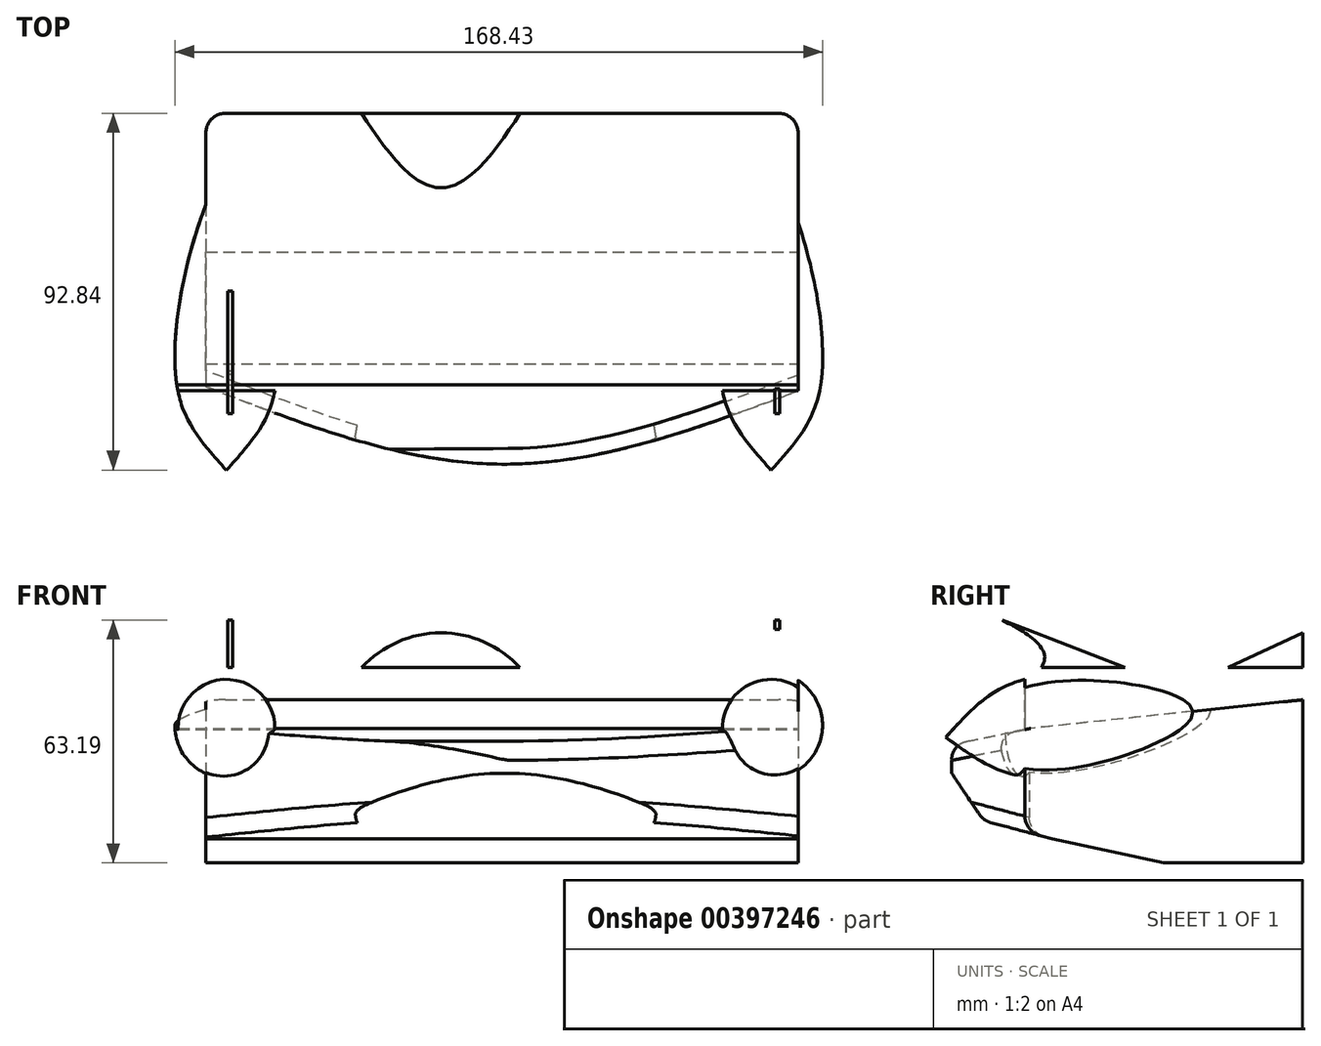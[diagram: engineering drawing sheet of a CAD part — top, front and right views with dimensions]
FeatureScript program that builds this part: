
annotation { "Feature Type Name" : "Feature", "Feature Type Description" : "" }
export const myFeature = defineFeature(function(context is Context, id is Id, definition is map)
    precondition{}
    {
        {
            var Q0;
            Q0=qCreatedBy(makeId("Top.planeOp"),FACE);
            var sketch = newSketch(context, id + "F0", { "sketchPlane" : qUnion([Q0])});
            skLineSegment(sketch, "E0.bottom", {"start": v(-78.1, 78.43) * mm, "end": v(75.9, 78.43) * mm});
            skLineSegment(sketch, "E0.top", {"start": v(-78.1, -12.86) * mm, "end": v(75.9, -12.86) * mm});
            skLineSegment(sketch, "E0.left", {"start": v(-78.1, 78.43) * mm, "end": v(-78.1, -12.86) * mm});
            skLineSegment(sketch, "E0.right", {"start": v(75.9, 78.43) * mm, "end": v(75.9, -12.86) * mm});
            skPoint(sketch, "E1", {"position": v(-1.1, -12.86) * mm});
            skFitSpline(sketch, "E2", {"points": [v(75.9, 6.2) * mm, v(-1.1, -12.86) * mm, v(-78.1, 7.33) * mm], "startDerivative": vector(-154.2, -57.78) * mm, "endDerivative": vector(-153.8, 60) * mm});
            skSolve(sketch);
        }
        {
            var Q0;
            Q0=makeQuery(id+"F0.imprint","IMPRINT",FACE,{"disambiguationData":[TD([[makeQuery(id+"F0.imprint","IMPRINT",EDGE,{"derivedFrom":sQuery(id+"F0.wireOp",EDGE,"E0.bottom")}),-1.0]])]});
            extrude(context, id + "F1", {"entities" : qUnion([Q0]), "depth" : 50.8 * mm});
        }
        {
            var Q0;
            Q0=makeQuery(id+"F1.opExtrude","SWEPT_FACE",FACE,{"disambiguationData":[OSD([sQuery(id+"F0.wireOp",EDGE,"E0.right")])]});
            var sketch = newSketch(context, id + "F2", { "sketchPlane" : qUnion([Q0])});
            skLineSegment(sketch, "E3.bottom", {"start": v(-17.29, 100.9) * mm, "end": v(100.26, 100.9) * mm});
            skLineSegment(sketch, "E3.top", {"start": v(-17.29, -25.48) * mm, "end": v(100.26, -25.48) * mm});
            skLineSegment(sketch, "E3.left", {"start": v(-17.29, 100.9) * mm, "end": v(-17.29, -25.48) * mm});
            skLineSegment(sketch, "E3.right", {"start": v(100.26, 100.9) * mm, "end": v(100.26, -25.48) * mm});
            skLineSegment(sketch, "E4", {"start": v(81.46, 42.76) * mm, "end": v(7.74, 35) * mm});
            skLineSegment(sketch, "E5", {"start": v(13.3, 6.25) * mm, "end": v(42.32, 0) * mm});
            skLineSegment(sketch, "E6", {"start": v(81.46, 42.76) * mm, "end": v(100.26, 42.76) * mm});
            skLineSegment(sketch, "E7", {"start": v(42.32, 0) * mm, "end": v(100.26, 0) * mm});
            skLineSegment(sketch, "E8", {"start": v(7.74, 35) * mm, "end": v(-17.29, 29.94) * mm});
            skLineSegment(sketch, "E9", {"start": v(-17.29, 29.94) * mm, "end": v(-4.57, 11.01) * mm});
            skLineSegment(sketch, "E10", {"start": v(-4.57, 11.01) * mm, "end": v(13.3, 6.25) * mm});
            skSolve(sketch);
        }
        {
            var Q0;
            {var subQ1=sQuery(id+"F2.wireOp",EDGE,"E3.bottom");Q0=makeQuery(id+"F2.imprint","IMPRINT",FACE,{"disambiguationData":[TD([[makeQuery(id+"F2.imprint","IMPRINT",EDGE,{"derivedFrom":subQ1}),-1.0]])]});}
            var Q1;
            {var subQ1=sQuery(id+"F2.wireOp",EDGE,"E3.top");Q1=makeQuery(id+"F2.imprint","IMPRINT",FACE,{"disambiguationData":[TD([[makeQuery(id+"F2.imprint","IMPRINT",EDGE,{"derivedFrom":subQ1}),1.0]])]});}
            var Q2;
            {var subQ0=sQuery(id+"F0.wireOp",EDGE,"E0.right");var subQ1=makeQuery(id+"F1.opExtrude","CAP_EDGE",EDGE,{"disambiguationData":[OSD([subQ0])],"isStart":false});Q2=makeQuery(id+"F2.imprint","IMPRINT",FACE,{"disambiguationData":[TD([[makeQuery(id+"F2.imprint","IMPRINT",EDGE,{"derivedFrom":subQ1}),1.0]])]});}
            var Q3;
            {var subQ0=sQuery(id+"F2.wireOp",EDGE,"E5");Q3=makeQuery(id+"F2.imprint","IMPRINT",FACE,{"disambiguationData":[TD([[makeQuery(id+"F2.imprint","IMPRINT",EDGE,{"derivedFrom":subQ0}),-1.0]])]});}
            extrude(context, id + "F3", {"entities" : qUnion([Q0, Q1, Q2, Q3]), "operationType" : NewBodyOperationType.REMOVE, "oppositeDirection" : true, "depth" : 177.8 * mm});
        }
        {
            var Q0;
            {var subQ0=sQuery(id+"F0.wireOp",EDGE,"E2");Q0=makeQuery(id+"F3.boolean.opBoolean","INTERSECT",EDGE,{"derivedFrom":[makeQuery(id+"F1.opExtrude","SWEPT_FACE",FACE,{"disambiguationData":[OSD([subQ0]),TDD([makeQuery(id+"F0.imprint","IMPRINT",EDGE,{"disambiguationData":[TD([[makeQuery(id+"F0.imprint","INTERSECT",VERTEX,{"derivedFrom":[sQuery(id+"F0.wireOp",EDGE,"E0.right"),subQ0]}),-1.0]])],"derivedFrom":subQ0})])]}),makeQuery(id+"F3.opExtrude","SWEPT_FACE",FACE,{"disambiguationData":[OSD([sQuery(id+"F2.wireOp",EDGE,"E8")])]})]});}
            var Q1;
            {var subQ0=sQuery(id+"F0.wireOp",EDGE,"E2");Q1=makeQuery(id+"F3.boolean.opBoolean","INTERSECT",EDGE,{"derivedFrom":[makeQuery(id+"F1.opExtrude","SWEPT_FACE",FACE,{"disambiguationData":[OSD([subQ0]),TDD([makeQuery(id+"F0.imprint","IMPRINT",EDGE,{"disambiguationData":[TD([[makeQuery(id+"F0.imprint","INTERSECT",VERTEX,{"derivedFrom":[sQuery(id+"F0.wireOp",EDGE,"E0.right"),subQ0]}),-1.0]])],"derivedFrom":subQ0})])]}),makeQuery(id+"F3.opExtrude","SWEPT_FACE",FACE,{"disambiguationData":[OSD([sQuery(id+"F2.wireOp",EDGE,"E10")])]})]});}
            var Q2;
            {var subQ0=sQuery(id+"F0.wireOp",EDGE,"E2");Q2=makeQuery(id+"F3.boolean.opBoolean","INTERSECT",EDGE,{"derivedFrom":[makeQuery(id+"F1.opExtrude","SWEPT_FACE",FACE,{"disambiguationData":[OSD([subQ0]),TDD([makeQuery(id+"F0.imprint","IMPRINT",EDGE,{"disambiguationData":[TD([[makeQuery(id+"F0.imprint","INTERSECT",VERTEX,{"derivedFrom":[sQuery(id+"F0.wireOp",EDGE,"E0.left"),subQ0]}),1.0]])],"derivedFrom":subQ0})])]}),makeQuery(id+"F3.opExtrude","SWEPT_FACE",FACE,{"disambiguationData":[OSD([sQuery(id+"F2.wireOp",EDGE,"E10")])]})]});}
            var Q3;
            Q3=makeQuery(id+"F3.boolean.opBoolean","COPY",EDGE,{"derivedFrom":makeQuery(id+"F3.opExtrude","SWEPT_EDGE",EDGE,{"disambiguationData":[OSD([sQuery(id+"F2.wireOp",EDGE,"E9"),sQuery(id+"F2.wireOp",EDGE,"E10")])]})});
            fillet(context, id + "F4", {"entities" : qUnion([Q0, Q1, Q2, Q3]), "radius" : 5.08 * mm, "tangentPropagation" : true, "allowEdgeOverflow" : false});
        }
        {
            var Q0;
            Q0=makeQuery(id+"F3.boolean.opBoolean","COPY",FACE,{"derivedFrom":makeQuery(id+"F3.opExtrude","SWEPT_FACE",FACE,{"disambiguationData":[OSD([sQuery(id+"F2.wireOp",EDGE,"E4")])]})});
            cPlane(context, id + "F5", {"entities" : qUnion([Q0]), "cplaneType" : CPlaneType.OFFSET, "offset" : 0 * mm, "oppositeDirection" : true, "width" : 152.4 * mm, "height" : 152.4 * mm});
        }
        {
            var Q0;
            Q0=qCreatedBy(id+"F5.planeOp",FACE);
            var sketch = newSketch(context, id + "F6", { "sketchPlane" : qUnion([Q0])});
            skLineSegment(sketch, "E11", {"start": v(-72.76, -10.91) * mm, "end": v(-72.76, 70.39) * mm});
            skFitSpline(sketch, "E12", {"points": [v(-72.76, 70.39) * mm, v(-85.7, 11.75) * mm, v(-72.76, -10.91) * mm], "startDerivative": vector(-49.44, -94.28) * mm, "endDerivative": vector(53.11, -59.52) * mm});
            skLineSegment(sketch, "E13", {"start": v(-1.95, 81.76) * mm, "end": v(-1.95, 38.21) * mm});
            skLineSegment(sketch, "E14.MirrorCS", {"start": v(68.85, -10.91) * mm, "end": v(68.85, 70.39) * mm});
            skFitSpline(sketch, "E15.MirrorCS", {"points": [v(68.85, 70.39) * mm, v(81.8, 11.75) * mm, v(68.85, -10.91) * mm], "startDerivative": vector(49.44, -94.28) * mm, "endDerivative": vector(-53.11, -59.52) * mm});
            skSolve(sketch);
        }
        {
            var Q0;
            Q0=makeQuery(id+"F6.imprint","IMPRINT",FACE,{"disambiguationData":[TD([[makeQuery(id+"F6.imprint","IMPRINT",EDGE,{"derivedFrom":sQuery(id+"F6.wireOp",EDGE,"E11")}),1.0]])]});
            var Q1;
            Q1=sQuery(id+"F6.wireOp",EDGE,"E11");
            revolve(context, id + "F7", {"operationType" : NewBodyOperationType.ADD, "entities" : qUnion([Q0]), "axis" : qUnion([Q1]), "revolveType" : RevolveType.FULL});
        }
        {
            var Q0;
            Q0=qCreatedBy(makeId("Right.planeOp"),FACE);
            cPlane(context, id + "F8", {"entities" : qUnion([Q0]), "cplaneType" : CPlaneType.OFFSET, "offset" : 69.85 * mm, "width" : 152.4 * mm, "height" : 152.4 * mm});
        }
        {
            var Q0;
            Q0=qCreatedBy(makeId("Right.planeOp"),FACE);
            var Q1;
            Q1=sQuery(id+"F6.wireOp",EDGE,"ea5a290e-ecb2-41d0-b12d-9c61fcfb37ff");
            cPlane(context, id + "F9", {"entities" : qUnion([Q0, Q1]), "cplaneType" : CPlaneType.OFFSET, "offset" : 72.39 * mm, "oppositeDirection" : true, "width" : 152.4 * mm, "height" : 152.4 * mm});
        }
        {
            var Q0;
            Q0=qCreatedBy(id+"F9.planeOp",FACE);
            var sketch = newSketch(context, id + "F10", { "sketchPlane" : qUnion([Q0])});
            skLineSegment(sketch, "E16.bottom", {"start": v(41.56, 42.66) * mm, "end": v(0.32, 42.66) * mm});
            skLineSegment(sketch, "E16.top", {"start": v(41.56, 63.19) * mm, "end": v(0.32, 63.19) * mm});
            skLineSegment(sketch, "E16.left", {"start": v(41.56, 42.66) * mm, "end": v(41.56, 63.19) * mm});
            skLineSegment(sketch, "E16.right", {"start": v(0.32, 42.66) * mm, "end": v(0.32, 63.19) * mm});
            skFitSpline(sketch, "E17", {"points": [v(0.32, 63.19) * mm, v(11.34, 53.5) * mm, v(0.32, 42.66) * mm], "startDerivative": vector(13.97, -7.25) * mm, "endDerivative": vector(-13.84, -8.47) * mm});
            skLineSegment(sketch, "E18", {"start": v(0.32, 63.19) * mm, "end": v(41.56, 47.17) * mm});
            skSolve(sketch);
        }
        {
            var Q0;
            Q0=makeQuery(id+"F10.imprint","IMPRINT",FACE,{"disambiguationData":[TD([[makeQuery(id+"F10.imprint","IMPRINT",EDGE,{"derivedFrom":sQuery(id+"F10.wireOp",EDGE,"E16.bottom")}),-1.0]])]});
            var sketch = newSketch(context, id + "F11", { "sketchPlane" : qUnion([Q0])});
            skSolve(sketch);
        }
        {
            var Q0;
            Q0=makeQuery(id+"F11.imprint","IMPRINT",FACE,{"disambiguationData":[TD([[makeQuery(id+"F11.imprint","IMPRINT",EDGE,{"derivedFrom":makeQuery(id+"F10.imprint","IMPRINT",EDGE,{"derivedFrom":sQuery(id+"F10.wireOp",EDGE,"E16.bottom")})}),-1.0]])]});
            extrude(context, id + "F12", {"entities" : qUnion([Q0]), "operationType" : NewBodyOperationType.ADD, "depth" : 1.27 * mm});
        }
        {
            var Q0;
            Q0=qCreatedBy(id+"F8.planeOp",FACE);
            var sketch = newSketch(context, id + "F13", { "sketchPlane" : qUnion([Q0])});
            skLineSegment(sketch, "E19.0.0", {"start": v(0.32, 63.19) * mm, "end": v(38.45, 48.38) * mm});
            skFitSpline(sketch, "E19.0.1", {"points": [v(38.45, 48.38) * mm, v(35.95, 48.73) * mm, v(32.19, 49.14) * mm, v(27.14, 49.46) * mm, v(23.36, 49.57) * mm, v(19.58, 49.53) * mm, v(15.81, 49.34) * mm, v(12.68, 49.02) * mm, v(10.19, 48.64) * mm, v(8.94, 48.4) * mm, v(8.32, 48.27) * mm]});
            skFitSpline(sketch, "E19.0.2", {"points": [v(0.32, 42.66) * mm, v(2.65, 44.1) * mm, v(20.04, 53.73) * mm, v(2.61, 62) * mm, v(0.32, 63.19) * mm]});
            skFitSpline(sketch, "E20.0", {"points": [v(0.32, 63.19) * mm, v(2.61, 62) * mm, v(20.04, 53.73) * mm, v(2.65, 44.1) * mm, v(0.32, 42.66) * mm]});
            skLineSegment(sketch, "E21.0", {"start": v(41.56, 42.66) * mm, "end": v(0.32, 42.66) * mm});
            skLineSegment(sketch, "E22.0", {"start": v(41.56, 42.66) * mm, "end": v(41.56, 63.19) * mm});
            skLineSegment(sketch, "E23.0", {"start": v(41.56, 63.19) * mm, "end": v(0.32, 63.19) * mm});
            skLineSegment(sketch, "E24.0", {"start": v(0.32, 42.66) * mm, "end": v(0.32, 63.19) * mm});
            skSolve(sketch);
        }
        {
            var Q0;
            {var subQ0=sQuery(id+"F13.wireOp",EDGE,"E19.0.0");Q0=makeQuery(id+"F13.imprint","IMPRINT",FACE,{"disambiguationData":[TD([[makeQuery(id+"F13.imprint","IMPRINT",EDGE,{"derivedFrom":subQ0}),-1.0]])]});}
            extrude(context, id + "F14", {"entities" : qUnion([Q0]), "operationType" : NewBodyOperationType.ADD, "depth" : 1.27 * mm});
        }
        {
            var Q0;
            Q0=makeQuery(id+"F6.imprint","IMPRINT",FACE,{"disambiguationData":[TD([[makeQuery(id+"F6.imprint","IMPRINT",EDGE,{"derivedFrom":sQuery(id+"F6.wireOp",EDGE,"E14.MirrorCS")}),-1.0]])]});
            var Q1;
            Q1=sQuery(id+"F6.wireOp",EDGE,"E14.MirrorCS");
            revolve(context, id + "F15", {"operationType" : NewBodyOperationType.ADD, "entities" : qUnion([Q0]), "axis" : qUnion([Q1]), "revolveType" : RevolveType.FULL});
        }
        {
            var Q0;
            Q0=makeQuery(id+"F1.opExtrude","SWEPT_EDGE",EDGE,{"disambiguationData":[OSD([sQuery(id+"F0.wireOp",EDGE,"E0.bottom"),sQuery(id+"F0.wireOp",EDGE,"E0.right")])]});
            var Q1;
            Q1=makeQuery(id+"F1.opExtrude","SWEPT_EDGE",EDGE,{"disambiguationData":[OSD([sQuery(id+"F0.wireOp",EDGE,"E0.bottom"),sQuery(id+"F0.wireOp",EDGE,"E0.left")])]});
            fillet(context, id + "F16", {"entities" : qUnion([Q0, Q1]), "radius" : 5.08 * mm, "tangentPropagation" : true, "allowEdgeOverflow" : false});
        }
        {
            var Q0;
            Q0=makeQuery(id+"F1.opExtrude","SWEPT_FACE",FACE,{"disambiguationData":[OSD([sQuery(id+"F0.wireOp",EDGE,"E0.bottom")])]});
            cPlane(context, id + "F17", {"entities" : qUnion([Q0]), "cplaneType" : CPlaneType.OFFSET, "offset" : 0 * mm, "width" : 152.4 * mm, "height" : 152.4 * mm});
        }
        {
            var Q0;
            Q0=qCreatedBy(id+"F17.planeOp",FACE);
            var sketch = newSketch(context, id + "F18", { "sketchPlane" : qUnion([Q0])});
            skCircle(sketch, "E25", {"center": v(16.98, 31.91) * mm, "radius": 27.93 * mm});
            skSolve(sketch);
        }
        {
            var Q0;
            Q0=makeQuery(id+"F18.imprint","IMPRINT",FACE,{"disambiguationData":[TD([[makeQuery(id+"F18.imprint","IMPRINT",EDGE,{"derivedFrom":sQuery(id+"F18.wireOp",EDGE,"E25")}),1.0]])]});
            extrude(context, id + "F19", {"entities" : qUnion([Q0]), "operationType" : NewBodyOperationType.ADD, "oppositeDirection" : true, "depth" : 50.8 * mm, "hasDraft" : true, "draftAngle" : 25 * degree, "draftPullDirection" : true});
        }
        {
            var Q0;
            {var subQ3=sQuery(id+"F2.wireOp",EDGE,"E4");Q0=makeQuery(id+"F2.imprint","IMPRINT",FACE,{"disambiguationData":[TD([[makeQuery(id+"F2.imprint","IMPRINT",EDGE,{"derivedFrom":subQ3}),-1.0]])]});}
            var Q1;
            {var subQ0=sQuery(id+"F2.wireOp",EDGE,"xj9Hy2z8-Rriq-Qvp7-IN8q-iiEjNOaLKhXj");Q1=makeQuery(id+"F2.imprint","IMPRINT",FACE,{"disambiguationData":[TD([[makeQuery(id+"F2.imprint","IMPRINT",EDGE,{"derivedFrom":subQ0}),-1.0]])]});}
            extrude(context, id + "F20", {"entities" : qUnion([Q0, Q1]), "operationType" : NewBodyOperationType.REMOVE, "oppositeDirection" : true, "depth" : 203.2 * mm});
        }
    });
